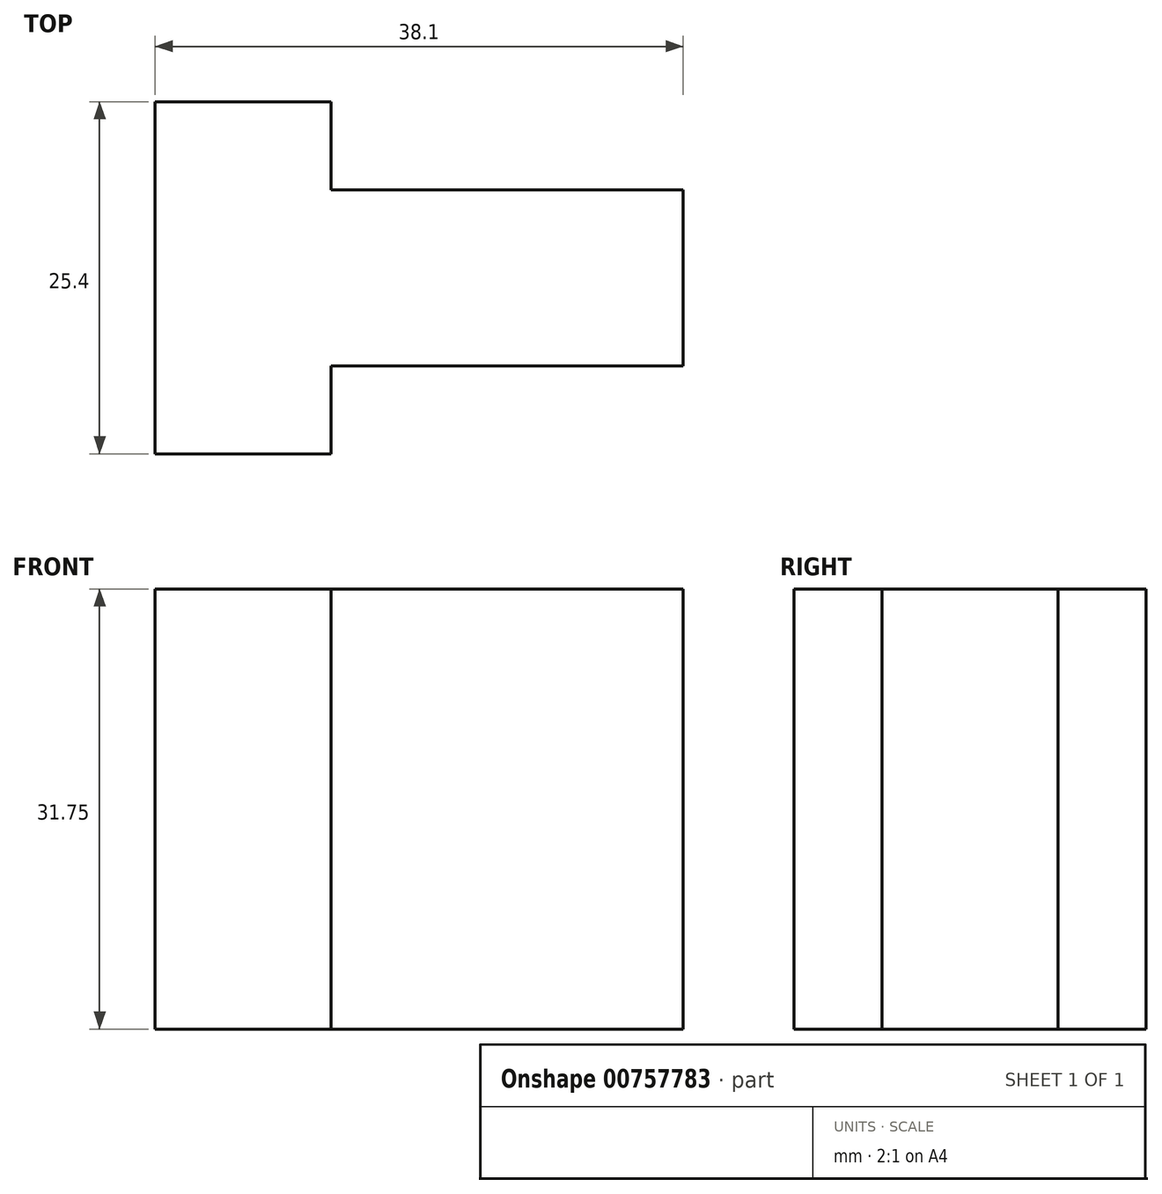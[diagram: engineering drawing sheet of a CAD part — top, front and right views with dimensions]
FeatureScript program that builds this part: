
annotation { "Feature Type Name" : "Feature", "Feature Type Description" : "" }
export const myFeature = defineFeature(function(context is Context, id is Id, definition is map)
    precondition{}
    {
        {
            var Q0;
            Q0=qCreatedBy(makeId("Front.planeOp"),FACE);
            var sketch = newSketch(context, id + "F0", { "sketchPlane" : qUnion([Q0])});
            skLineSegment(sketch, "E0", {"start": v(-19.53, 0) * mm, "end": v(18.57, 0) * mm});
            skLineSegment(sketch, "E1", {"start": v(18.57, 0) * mm, "end": v(18.57, 31.75) * mm});
            skLineSegment(sketch, "E2", {"start": v(18.57, 31.75) * mm, "end": v(-19.53, 31.75) * mm});
            skLineSegment(sketch, "E3", {"start": v(-19.53, 31.75) * mm, "end": v(-19.53, 0) * mm});
            skSolve(sketch);
        }
        {
            var Q0;
            Q0 = qSketchRegion(id + "F0", true);
            extrude(context, id + "F1", {"entities" : qUnion([Q0]), "depth" : 25.4 * mm, "offsetDistance" : 25.4 * mm});
        }
        {
            var Q0;
            Q0=makeQuery(id+"F1.opExtrude","SWEPT_FACE",FACE,{"disambiguationData":[OSD([sQuery(id+"F0.wireOp",EDGE,"E2")])]});
            var sketch = newSketch(context, id + "F2", { "sketchPlane" : qUnion([Q0])});
            skLineSegment(sketch, "E4", {"start": v(-6.83, -25.4) * mm, "end": v(-6.83, -19.05) * mm});
            skLineSegment(sketch, "E5", {"start": v(-6.83, -19.05) * mm, "end": v(18.57, -19.05) * mm});
            skLineSegment(sketch, "E6", {"start": v(18.57, -19.05) * mm, "end": v(18.57, -6.35) * mm});
            skLineSegment(sketch, "E7", {"start": v(18.57, -6.35) * mm, "end": v(-6.83, -6.35) * mm});
            skLineSegment(sketch, "E8", {"start": v(-6.83, -6.35) * mm, "end": v(-6.83, 0) * mm});
            skSolve(sketch);
        }
        {
            var Q0;
            Q0 = qSketchRegion(id + "F2", true);
            var Q1;
            {var subQ0=sQuery(id+"F2.wireOp",EDGE,"E4");Q1=makeQuery(id+"F2.imprint","IMPRINT",FACE,{"disambiguationData":[TD([[makeQuery(id+"F2.imprint","IMPRINT",EDGE,{"derivedFrom":subQ0}),-1.0]])]});}
            var Q2;
            {var subQ0=sQuery(id+"F2.wireOp",EDGE,"E7");Q2=makeQuery(id+"F2.imprint","IMPRINT",FACE,{"disambiguationData":[TD([[makeQuery(id+"F2.imprint","IMPRINT",EDGE,{"derivedFrom":subQ0}),-1.0]])]});}
            extrude(context, id + "F3", {"entities" : qUnion([Q0, Q1, Q2]), "operationType" : NewBodyOperationType.REMOVE, "endBound" : BoundingType.THROUGH_ALL, "oppositeDirection" : true, "depth" : 25.4 * mm, "offsetDistance" : 25.4 * mm});
        }
    });
